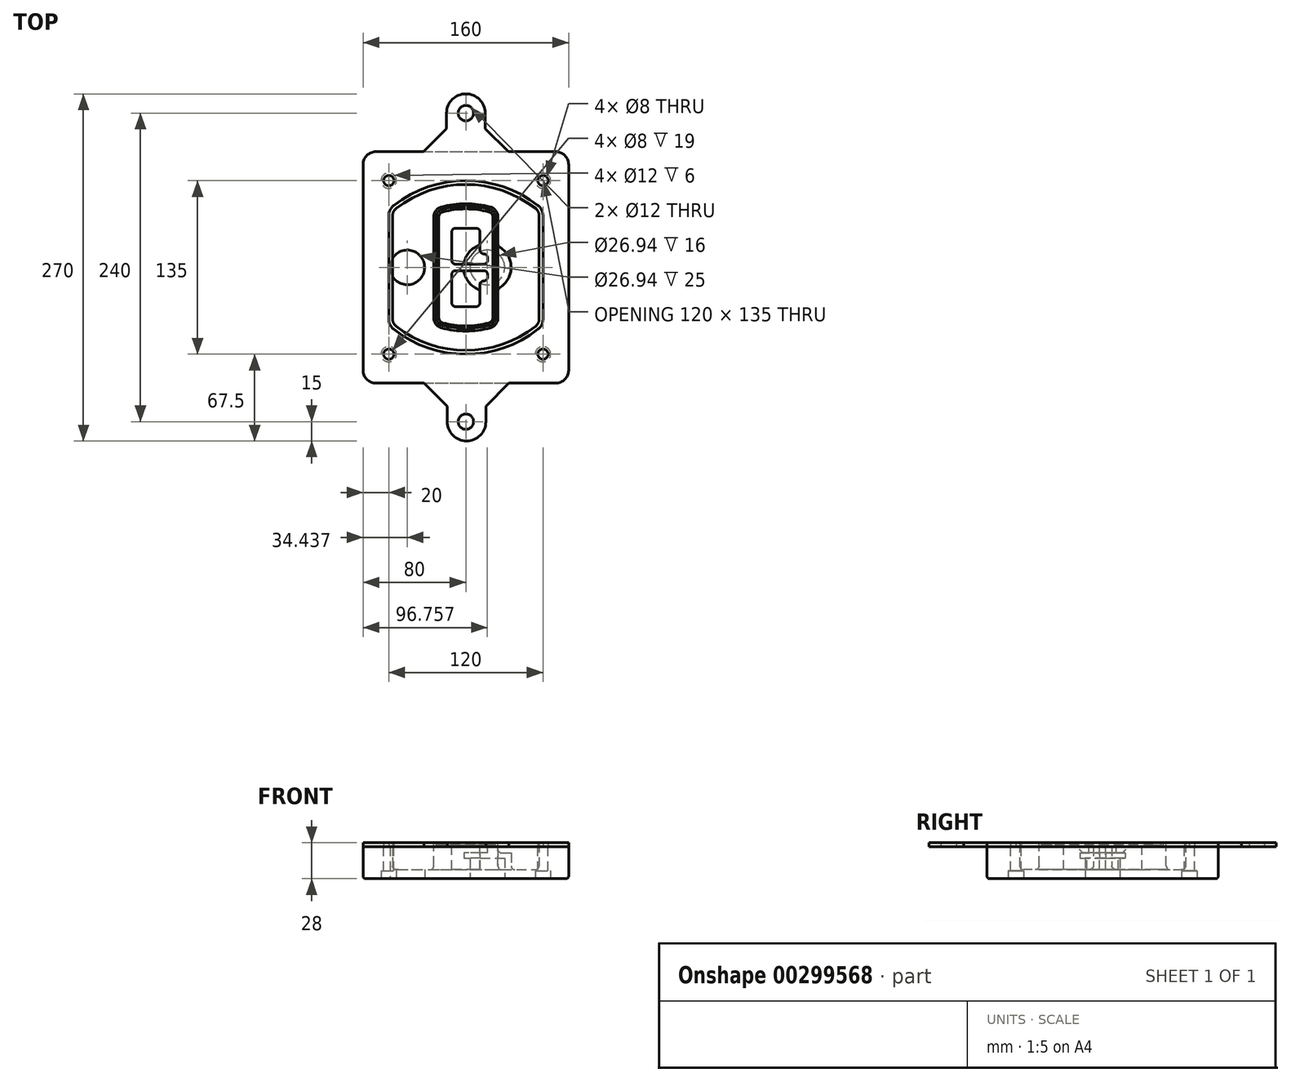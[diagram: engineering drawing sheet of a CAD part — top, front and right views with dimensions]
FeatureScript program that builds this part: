
annotation { "Feature Type Name" : "Feature", "Feature Type Description" : "" }
export const myFeature = defineFeature(function(context is Context, id is Id, definition is map)
    precondition{}
    {
        {
            var Q0;
            Q0=qCreatedBy(makeId("Top.planeOp"),FACE);
            var sketch = newSketch(context, id + "F0", { "sketchPlane" : qUnion([Q0])});
            skPoint(sketch, "E0.rect.middle", {"position": v(0, 0) * mm});
            skLineSegment(sketch, "E1.bottom", {"start": v(-70, -90) * mm, "end": v(70, -90) * mm});
            skLineSegment(sketch, "E1.top", {"start": v(-70, 90) * mm, "end": v(70, 90) * mm});
            skLineSegment(sketch, "E1.left", {"start": v(-80, -80) * mm, "end": v(-80, 80) * mm});
            skLineSegment(sketch, "E1.right", {"start": v(80, -80) * mm, "end": v(80, 80) * mm});
            skLineSegment(sketch, "E2", {"start": v(-80, 90) * mm, "end": v(80, -90) * mm, "construction": true});
            skLineSegment(sketch, "E3", {"start": v(80, 90) * mm, "end": v(-80, -90) * mm, "construction": true});
            skCircle(sketch, "E4", {"center": v(-60, 67.5) * mm, "radius": 4 * mm});
            skCircle(sketch, "E5", {"center": v(60, 67.5) * mm, "radius": 4 * mm});
            skCircle(sketch, "E6", {"center": v(60, -67.5) * mm, "radius": 4 * mm});
            skCircle(sketch, "E7", {"center": v(-60, -67.5) * mm, "radius": 4 * mm});
            skLineSegment(sketch, "E8", {"start": v(-60, 67.5) * mm, "end": v(60, 67.5) * mm, "construction": true});
            skLineSegment(sketch, "E9", {"start": v(60, 67.5) * mm, "end": v(60, -67.5) * mm, "construction": true});
            skLineSegment(sketch, "E10", {"start": v(60, -67.5) * mm, "end": v(-60, -67.5) * mm, "construction": true});
            skLineSegment(sketch, "E11", {"start": v(-60, -67.5) * mm, "end": v(-60, 67.5) * mm, "construction": true});
            skLineSegment(sketch, "E12", {"start": v(-60, 40.3) * mm, "end": v(-60, -40.3) * mm});
            skLineSegment(sketch, "E13", {"start": v(60, 40.3) * mm, "end": v(60, -40.3) * mm});
            skArc(sketch, "E14", {"start": v(56.15, 48.18) * mm, "mid": v(0, 67.5) * mm, "end": v(-56.15, 48.18) * mm});
            skArc(sketch, "E15", {"start": v(-56.15, -48.18) * mm, "mid": v(0, -67.5) * mm, "end": v(56.15, -48.18) * mm});
            skLineSegment(sketch, "E16", {"start": v(-60, 0) * mm, "end": v(60, 0) * mm, "construction": true});
            skPoint(sketch, "E17.visualSharp", {"position": v(-60, -45) * mm});
            skArc(sketch, "E17.filletArc", {"start": v(-60, -40.3) * mm, "mid": v(-58.99, -44.68) * mm, "end": v(-56.15, -48.18) * mm});
            skPoint(sketch, "E18.visualSharp", {"position": v(-60, 45) * mm});
            skArc(sketch, "E18.filletArc", {"start": v(-56.15, 48.18) * mm, "mid": v(-58.99, 44.68) * mm, "end": v(-60, 40.3) * mm});
            skPoint(sketch, "E19.visualSharp", {"position": v(60, 45) * mm});
            skArc(sketch, "E19.filletArc", {"start": v(60, 40.3) * mm, "mid": v(58.99, 44.68) * mm, "end": v(56.15, 48.18) * mm});
            skPoint(sketch, "E20.visualSharp", {"position": v(60, -45) * mm});
            skArc(sketch, "E20.filletArc", {"start": v(56.15, -48.18) * mm, "mid": v(58.99, -44.68) * mm, "end": v(60, -40.3) * mm});
            skPoint(sketch, "E21.visualSharp", {"position": v(-80, 90) * mm});
            skArc(sketch, "E21.filletArc", {"start": v(-70, 90) * mm, "mid": v(-77.07, 87.07) * mm, "end": v(-80, 80) * mm});
            skPoint(sketch, "E22.visualSharp", {"position": v(80, 90) * mm});
            skArc(sketch, "E22.filletArc", {"start": v(80, 80) * mm, "mid": v(77.07, 87.07) * mm, "end": v(70, 90) * mm});
            skPoint(sketch, "E23.visualSharp", {"position": v(80, -90) * mm});
            skArc(sketch, "E23.filletArc", {"start": v(70, -90) * mm, "mid": v(77.07, -87.07) * mm, "end": v(80, -80) * mm});
            skPoint(sketch, "E24.visualSharp", {"position": v(-80, -90) * mm});
            skArc(sketch, "E24.filletArc", {"start": v(-80, -80) * mm, "mid": v(-77.07, -87.07) * mm, "end": v(-70, -90) * mm});
            skArc(sketch, "E25.0", {"start": v(57, 40.3) * mm, "mid": v(56.3, 43.36) * mm, "end": v(54.3, 45.81) * mm});
            skLineSegment(sketch, "E25.1", {"start": v(57, 40.3) * mm, "end": v(57, -40.3) * mm});
            skArc(sketch, "E25.2", {"start": v(54.3, -45.81) * mm, "mid": v(56.3, -43.36) * mm, "end": v(57, -40.3) * mm});
            skArc(sketch, "E25.3", {"start": v(-54.3, -45.81) * mm, "mid": v(0, -64.5) * mm, "end": v(54.3, -45.81) * mm});
            skArc(sketch, "E25.4", {"start": v(-57, -40.3) * mm, "mid": v(-56.3, -43.36) * mm, "end": v(-54.3, -45.81) * mm});
            skArc(sketch, "E25.5", {"start": v(54.3, 45.81) * mm, "mid": v(0, 64.5) * mm, "end": v(-54.3, 45.81) * mm});
            skLineSegment(sketch, "E25.6", {"start": v(-57, 40.3) * mm, "end": v(-57, -40.3) * mm});
            skArc(sketch, "E25.7", {"start": v(-54.3, 45.81) * mm, "mid": v(-56.3, 43.36) * mm, "end": v(-57, 40.3) * mm});
            skArc(sketch, "E26.0", {"start": v(-58.62, 51.33) * mm, "mid": v(-62.58, 46.43) * mm, "end": v(-64, 40.3) * mm});
            skArc(sketch, "E26.1", {"start": v(58.62, 51.33) * mm, "mid": v(0, 71.5) * mm, "end": v(-58.62, 51.33) * mm});
            skArc(sketch, "E26.2", {"start": v(64, 40.3) * mm, "mid": v(62.58, 46.43) * mm, "end": v(58.62, 51.33) * mm});
            skLineSegment(sketch, "E26.3", {"start": v(64, 40.3) * mm, "end": v(64, -40.3) * mm});
            skArc(sketch, "E26.4", {"start": v(58.62, -51.33) * mm, "mid": v(62.58, -46.43) * mm, "end": v(64, -40.3) * mm});
            skLineSegment(sketch, "E26.5", {"start": v(-64, 40.3) * mm, "end": v(-64, -40.3) * mm});
            skArc(sketch, "E26.6", {"start": v(-58.62, -51.33) * mm, "mid": v(0, -71.5) * mm, "end": v(58.62, -51.33) * mm});
            skArc(sketch, "E26.7", {"start": v(-64, -40.3) * mm, "mid": v(-62.58, -46.43) * mm, "end": v(-58.62, -51.33) * mm});
            skSolve(sketch);
        }
        {
            var Q0;
            Q0=makeQuery(id+"F0.imprint","IMPRINT",FACE,{"disambiguationData":[TD([[makeQuery(id+"F0.imprint","IMPRINT",EDGE,{"derivedFrom":sQuery(id+"F0.wireOp",EDGE,"E1.bottom")}),1.0]])]});
            var Q1;
            Q1=makeQuery(id+"F0.imprint","IMPRINT",FACE,{"disambiguationData":[TD([[makeQuery(id+"F0.imprint","IMPRINT",EDGE,{"derivedFrom":sQuery(id+"F0.wireOp",EDGE,"E12")}),1.0]])]});
            var Q2;
            Q2=makeQuery(id+"F0.imprint","IMPRINT",FACE,{"disambiguationData":[TD([[makeQuery(id+"F0.imprint","IMPRINT",EDGE,{"derivedFrom":sQuery(id+"F0.wireOp",EDGE,"E25.0")}),1.0]])]});
            var Q3;
            Q3=makeQuery(id+"F0.imprint","IMPRINT",FACE,{"disambiguationData":[TD([[makeQuery(id+"F0.imprint","IMPRINT",EDGE,{"derivedFrom":sQuery(id+"F0.wireOp",EDGE,"E12")}),-1.0]])]});
            extrude(context, id + "F1", {"entities" : qUnion([Q0, Q1, Q2, Q3]), "oppositeDirection" : true, "depth" : 25 * mm});
        }
        {
            var Q0;
            Q0=makeQuery(id+"F0.imprint","IMPRINT",FACE,{"disambiguationData":[TD([[makeQuery(id+"F0.imprint","IMPRINT",EDGE,{"derivedFrom":sQuery(id+"F0.wireOp",EDGE,"E12")}),1.0]])]});
            extrude(context, id + "F2", {"entities" : qUnion([Q0]), "operationType" : NewBodyOperationType.ADD, "depth" : 3 * mm});
        }
        {
            var Q0;
            Q0=makeQuery(id+"F0.imprint","IMPRINT",FACE,{"disambiguationData":[TD([[makeQuery(id+"F0.imprint","IMPRINT",EDGE,{"derivedFrom":sQuery(id+"F0.wireOp",EDGE,"E25.0")}),1.0]])]});
            extrude(context, id + "F3", {"entities" : qUnion([Q0]), "operationType" : NewBodyOperationType.REMOVE, "oppositeDirection" : true, "depth" : 18 * mm});
        }
        {
            var Q0;
            Q0=makeQuery(id+"F2.opExtrude","CAP_FACE",FACE,{"disambiguationData":[OSD([sQuery(id+"F0.wireOp",EDGE,"E12"),sQuery(id+"F0.wireOp",EDGE,"E13"),sQuery(id+"F0.wireOp",EDGE,"E14"),sQuery(id+"F0.wireOp",EDGE,"E15"),sQuery(id+"F0.wireOp",EDGE,"E17.filletArc"),sQuery(id+"F0.wireOp",EDGE,"E18.filletArc"),sQuery(id+"F0.wireOp",EDGE,"E19.filletArc"),sQuery(id+"F0.wireOp",EDGE,"E20.filletArc"),sQuery(id+"F0.wireOp",EDGE,"E25.0"),sQuery(id+"F0.wireOp",EDGE,"E25.1"),sQuery(id+"F0.wireOp",EDGE,"E25.2"),sQuery(id+"F0.wireOp",EDGE,"E25.3"),sQuery(id+"F0.wireOp",EDGE,"E25.4"),sQuery(id+"F0.wireOp",EDGE,"E25.5"),sQuery(id+"F0.wireOp",EDGE,"E25.6"),sQuery(id+"F0.wireOp",EDGE,"E25.7")])],"isStart":false});
            var sketch = newSketch(context, id + "F4", { "sketchPlane" : qUnion([Q0])});
            skArc(sketch, "E27.0", {"start": v(-19.08, -46.97) * mm, "mid": v(0, -49.5) * mm, "end": v(19.08, -46.97) * mm});
            skArc(sketch, "E28.0", {"start": v(19.08, 46.97) * mm, "mid": v(0, 49.5) * mm, "end": v(-19.08, 46.97) * mm});
            skLineSegment(sketch, "E29", {"start": v(-25, 39.25) * mm, "end": v(-25, -39.25) * mm});
            skLineSegment(sketch, "E30", {"start": v(25, 39.25) * mm, "end": v(25, -39.25) * mm});
            skLineSegment(sketch, "E31", {"start": v(-25, 45.1) * mm, "end": v(25, 45.1) * mm, "construction": true});
            skLineSegment(sketch, "E32", {"start": v(-25, -45.1) * mm, "end": v(25, -45.1) * mm, "construction": true});
            skPoint(sketch, "E33.visualSharp", {"position": v(-25, 45.1) * mm});
            skArc(sketch, "E33.filletArc", {"start": v(-19.08, 46.97) * mm, "mid": v(-23.35, 44.11) * mm, "end": v(-25, 39.25) * mm});
            skPoint(sketch, "E34.visualSharp", {"position": v(25, 45.1) * mm});
            skArc(sketch, "E34.filletArc", {"start": v(25, 39.25) * mm, "mid": v(23.35, 44.11) * mm, "end": v(19.08, 46.97) * mm});
            skPoint(sketch, "E35.visualSharp", {"position": v(25, -45.1) * mm});
            skArc(sketch, "E35.filletArc", {"start": v(19.08, -46.97) * mm, "mid": v(23.35, -44.11) * mm, "end": v(25, -39.25) * mm});
            skPoint(sketch, "E36.visualSharp", {"position": v(-25, -45.1) * mm});
            skArc(sketch, "E36.filletArc", {"start": v(-25, -39.25) * mm, "mid": v(-23.35, -44.11) * mm, "end": v(-19.08, -46.97) * mm});
            skArc(sketch, "E37.0", {"start": v(54.3, 45.81) * mm, "mid": v(0, 64.5) * mm, "end": v(-54.3, 45.81) * mm});
            skArc(sketch, "E37.1", {"start": v(-54.3, 45.81) * mm, "mid": v(-56.3, 43.36) * mm, "end": v(-57, 40.3) * mm});
            skLineSegment(sketch, "E37.2", {"start": v(-57, 40.3) * mm, "end": v(-57, -40.3) * mm});
            skArc(sketch, "E37.3", {"start": v(-57, -40.3) * mm, "mid": v(-56.3, -43.36) * mm, "end": v(-54.3, -45.81) * mm});
            skArc(sketch, "E37.4", {"start": v(-54.3, -45.81) * mm, "mid": v(0, -64.5) * mm, "end": v(54.3, -45.81) * mm});
            skArc(sketch, "E37.5", {"start": v(54.3, -45.81) * mm, "mid": v(56.3, -43.36) * mm, "end": v(57, -40.3) * mm});
            skLineSegment(sketch, "E37.6", {"start": v(57, 40.3) * mm, "end": v(57, -40.3) * mm});
            skArc(sketch, "E37.7", {"start": v(57, 40.3) * mm, "mid": v(56.3, 43.36) * mm, "end": v(54.3, 45.81) * mm});
            skLineSegment(sketch, "E38.0", {"start": v(23, 39.25) * mm, "end": v(23, -39.25) * mm});
            skArc(sketch, "E38.1", {"start": v(18.56, -45.04) * mm, "mid": v(21.76, -42.9) * mm, "end": v(23, -39.25) * mm});
            skArc(sketch, "E38.2", {"start": v(-18.56, -45.04) * mm, "mid": v(0, -47.5) * mm, "end": v(18.56, -45.04) * mm});
            skArc(sketch, "E38.3", {"start": v(-23, -39.25) * mm, "mid": v(-21.76, -42.9) * mm, "end": v(-18.56, -45.04) * mm});
            skLineSegment(sketch, "E38.4", {"start": v(-23, 39.25) * mm, "end": v(-23, -39.25) * mm});
            skArc(sketch, "E38.5", {"start": v(23, 39.25) * mm, "mid": v(21.76, 42.9) * mm, "end": v(18.56, 45.04) * mm});
            skArc(sketch, "E38.6", {"start": v(-18.56, 45.04) * mm, "mid": v(-21.76, 42.9) * mm, "end": v(-23, 39.25) * mm});
            skArc(sketch, "E38.7", {"start": v(18.56, 45.04) * mm, "mid": v(0, 47.5) * mm, "end": v(-18.56, 45.04) * mm});
            skArc(sketch, "E39.0", {"start": v(21, 39.25) * mm, "mid": v(20.18, 41.68) * mm, "end": v(18.04, 43.1) * mm});
            skLineSegment(sketch, "E39.1", {"start": v(21, 39.25) * mm, "end": v(21, -39.25) * mm});
            skArc(sketch, "E39.2", {"start": v(18.04, -43.1) * mm, "mid": v(20.18, -41.68) * mm, "end": v(21, -39.25) * mm});
            skArc(sketch, "E39.3", {"start": v(-18.04, -43.1) * mm, "mid": v(0, -45.5) * mm, "end": v(18.04, -43.1) * mm});
            skArc(sketch, "E39.4", {"start": v(-21, -39.25) * mm, "mid": v(-20.18, -41.68) * mm, "end": v(-18.04, -43.1) * mm});
            skArc(sketch, "E39.5", {"start": v(18.04, 43.1) * mm, "mid": v(0, 45.5) * mm, "end": v(-18.04, 43.1) * mm});
            skLineSegment(sketch, "E39.6", {"start": v(-21, 39.25) * mm, "end": v(-21, -39.25) * mm});
            skArc(sketch, "E39.7", {"start": v(-18.04, 43.1) * mm, "mid": v(-20.18, 41.68) * mm, "end": v(-21, 39.25) * mm});
            skLineSegment(sketch, "E40", {"start": v(-25, 0) * mm, "end": v(25, 0) * mm, "construction": true});
            skLineSegment(sketch, "E41", {"start": v(-11, 5.5) * mm, "end": v(-11, 27.5) * mm});
            skLineSegment(sketch, "E42", {"start": v(-8, 30.5) * mm, "end": v(8, 30.5) * mm});
            skLineSegment(sketch, "E43", {"start": v(11, 27.5) * mm, "end": v(11, 13.5) * mm});
            skLineSegment(sketch, "E44", {"start": v(14, 10.5) * mm, "end": v(14, 10.5) * mm});
            skLineSegment(sketch, "E45", {"start": v(17, 7.5) * mm, "end": v(17, 5.5) * mm});
            skLineSegment(sketch, "E46", {"start": v(14, 2.5) * mm, "end": v(-8, 2.5) * mm});
            skPoint(sketch, "E47.visualSharp", {"position": v(-11, 30.5) * mm});
            skArc(sketch, "E47.filletArc", {"start": v(-8, 30.5) * mm, "mid": v(-10.12, 29.62) * mm, "end": v(-11, 27.5) * mm});
            skPoint(sketch, "E48.visualSharp", {"position": v(11, 30.5) * mm});
            skArc(sketch, "E48.filletArc", {"start": v(11, 27.5) * mm, "mid": v(10.12, 29.62) * mm, "end": v(8, 30.5) * mm});
            skPoint(sketch, "E49.visualSharp", {"position": v(11, 10.5) * mm});
            skArc(sketch, "E49.filletArc", {"start": v(11, 13.5) * mm, "mid": v(11.88, 11.38) * mm, "end": v(14, 10.5) * mm});
            skPoint(sketch, "E50.visualSharp", {"position": v(17, 10.5) * mm});
            skArc(sketch, "E50.filletArc", {"start": v(17, 7.5) * mm, "mid": v(16.12, 9.62) * mm, "end": v(14, 10.5) * mm});
            skPoint(sketch, "E51.visualSharp", {"position": v(17, 2.5) * mm});
            skArc(sketch, "E51.filletArc", {"start": v(14, 2.5) * mm, "mid": v(16.12, 3.38) * mm, "end": v(17, 5.5) * mm});
            skPoint(sketch, "E52.visualSharp", {"position": v(-11, 2.5) * mm});
            skArc(sketch, "E52.filletArc", {"start": v(-11, 5.5) * mm, "mid": v(-10.12, 3.38) * mm, "end": v(-8, 2.5) * mm});
            skLineSegment(sketch, "E53.0.MirrorCS", {"start": v(14, -2.5) * mm, "end": v(-8, -2.5) * mm});
            skArc(sketch, "E54.0.MirrorCS", {"start": v(-11, -5.5) * mm, "mid": v(-10.12, -3.38) * mm, "end": v(-8, -2.5) * mm});
            skLineSegment(sketch, "E55.0.MirrorCS", {"start": v(-11, -5.5) * mm, "end": v(-11, -27.5) * mm});
            skArc(sketch, "E56.0.MirrorCS", {"start": v(-8, -30.5) * mm, "mid": v(-10.12, -29.62) * mm, "end": v(-11, -27.5) * mm});
            skLineSegment(sketch, "E57.0.MirrorCS", {"start": v(-8, -30.5) * mm, "end": v(8, -30.5) * mm});
            skArc(sketch, "E58.0.MirrorCS", {"start": v(11, -27.5) * mm, "mid": v(10.12, -29.62) * mm, "end": v(8, -30.5) * mm});
            skLineSegment(sketch, "E59.0.MirrorCS", {"start": v(11, -27.5) * mm, "end": v(11, -13.5) * mm});
            skArc(sketch, "E60.0.MirrorCS", {"start": v(11, -13.5) * mm, "mid": v(11.88, -11.38) * mm, "end": v(14, -10.5) * mm});
            skArc(sketch, "E61.0.MirrorCS", {"start": v(17, -7.5) * mm, "mid": v(16.12, -9.62) * mm, "end": v(14, -10.5) * mm});
            skLineSegment(sketch, "E62.0.MirrorCS", {"start": v(17, -7.5) * mm, "end": v(17, -5.5) * mm});
            skArc(sketch, "E63.0.MirrorCS", {"start": v(14, -2.5) * mm, "mid": v(16.12, -3.38) * mm, "end": v(17, -5.5) * mm});
            skSolve(sketch);
        }
        {
            var Q0;
            Q0=makeQuery(id+"F4.imprint","IMPRINT",FACE,{"disambiguationData":[TD([[makeQuery(id+"F4.imprint","IMPRINT",EDGE,{"derivedFrom":sQuery(id+"F4.wireOp",EDGE,"E27.0")}),1.0]])]});
            var Q1;
            Q1=makeQuery(id+"F4.imprint","IMPRINT",FACE,{"disambiguationData":[TD([[makeQuery(id+"F4.imprint","IMPRINT",EDGE,{"derivedFrom":sQuery(id+"F4.wireOp",EDGE,"E38.0")}),-1.0]])]});
            var Q2;
            Q2=makeQuery(id+"F4.imprint","IMPRINT",FACE,{"disambiguationData":[TD([[makeQuery(id+"F4.imprint","IMPRINT",EDGE,{"derivedFrom":sQuery(id+"F4.wireOp",EDGE,"E39.0")}),1.0]])]});
            extrude(context, id + "F5", {"entities" : qUnion([Q0, Q1, Q2]), "operationType" : NewBodyOperationType.ADD, "endBound" : BoundingType.UP_TO_NEXT, "oppositeDirection" : true, "depth" : 25 * mm});
        }
        {
            var Q0;
            Q0=makeQuery(id+"F4.imprint","IMPRINT",FACE,{"disambiguationData":[TD([[makeQuery(id+"F4.imprint","IMPRINT",EDGE,{"derivedFrom":sQuery(id+"F4.wireOp",EDGE,"E38.0")}),-1.0]])]});
            extrude(context, id + "F6", {"entities" : qUnion([Q0]), "operationType" : NewBodyOperationType.REMOVE, "oppositeDirection" : true, "depth" : 2 * mm});
        }
        {
            var Q0;
            Q0=makeQuery(id+"F1.opExtrude","CAP_FACE",FACE,{"disambiguationData":[OSD([sQuery(id+"F0.wireOp",EDGE,"E1.bottom"),sQuery(id+"F0.wireOp",EDGE,"E1.top"),sQuery(id+"F0.wireOp",EDGE,"E1.left"),sQuery(id+"F0.wireOp",EDGE,"E1.right"),sQuery(id+"F0.wireOp",EDGE,"E4"),sQuery(id+"F0.wireOp",EDGE,"E5"),sQuery(id+"F0.wireOp",EDGE,"E6"),sQuery(id+"F0.wireOp",EDGE,"E7"),sQuery(id+"F0.wireOp",EDGE,"E21.filletArc"),sQuery(id+"F0.wireOp",EDGE,"E22.filletArc"),sQuery(id+"F0.wireOp",EDGE,"E23.filletArc"),sQuery(id+"F0.wireOp",EDGE,"E24.filletArc")])],"isStart":false});
            var sketch = newSketch(context, id + "F7", { "sketchPlane" : qUnion([Q0])});
            skCircle(sketch, "E64", {"center": v(16.76, 0) * mm, "radius": 13.47 * mm});
            skCircle(sketch, "E65", {"center": v(-45.56, 0) * mm, "radius": 13.47 * mm});
            skLineSegment(sketch, "E66", {"start": v(80, 0) * mm, "end": v(-80, 0) * mm});
            skCircle(sketch, "E67", {"center": v(16.76, 0) * mm, "radius": 18.47 * mm});
            skCircle(sketch, "E68", {"center": v(60, -67.5) * mm, "radius": 6 * mm});
            skCircle(sketch, "E69", {"center": v(-60, -67.5) * mm, "radius": 6 * mm});
            skCircle(sketch, "E70", {"center": v(-60, 67.5) * mm, "radius": 6 * mm});
            skCircle(sketch, "E71", {"center": v(60, 67.5) * mm, "radius": 6 * mm});
            skSolve(sketch);
        }
        {
            var Q0;
            {var subQ1=sQuery(id+"F7.wireOp",EDGE,"E66");var subQ4=sQuery(id+"F7.wireOp",EDGE,"E64");var subQ6=makeQuery(id+"F7.imprint","INTERSECT",VERTEX,{"disambiguationData":[OD(0.0)],"derivedFrom":[subQ4,subQ1]});Q0=makeQuery(id+"F7.imprint","IMPRINT",FACE,{"disambiguationData":[TD([[makeQuery(id+"F7.imprint","IMPRINT",EDGE,{"disambiguationData":[TD([[subQ6,-1.0]])],"derivedFrom":subQ4}),-1.0]])]});}
            var Q1;
            {var subQ0=sQuery(id+"F7.wireOp",EDGE,"E66");var subQ1=sQuery(id+"F7.wireOp",EDGE,"E64");var subQ3=makeQuery(id+"F7.imprint","INTERSECT",VERTEX,{"disambiguationData":[OD(0.0)],"derivedFrom":[subQ1,subQ0]});Q1=makeQuery(id+"F7.imprint","IMPRINT",FACE,{"disambiguationData":[TD([[makeQuery(id+"F7.imprint","IMPRINT",EDGE,{"disambiguationData":[TD([[subQ3,-1.0]])],"derivedFrom":subQ1}),1.0]])]});}
            var Q2;
            {var subQ0=sQuery(id+"F7.wireOp",EDGE,"E66");var subQ1=sQuery(id+"F7.wireOp",EDGE,"E64");var subQ3=makeQuery(id+"F7.imprint","INTERSECT",VERTEX,{"disambiguationData":[OD(0.0)],"derivedFrom":[subQ1,subQ0]});Q2=makeQuery(id+"F7.imprint","IMPRINT",FACE,{"disambiguationData":[TD([[makeQuery(id+"F7.imprint","IMPRINT",EDGE,{"disambiguationData":[TD([[subQ3,1.0]])],"derivedFrom":subQ1}),1.0]])]});}
            var Q3;
            {var subQ1=sQuery(id+"F7.wireOp",EDGE,"E66");var subQ4=sQuery(id+"F7.wireOp",EDGE,"E64");var subQ6=makeQuery(id+"F7.imprint","INTERSECT",VERTEX,{"disambiguationData":[OD(0.0)],"derivedFrom":[subQ4,subQ1]});Q3=makeQuery(id+"F7.imprint","IMPRINT",FACE,{"disambiguationData":[TD([[makeQuery(id+"F7.imprint","IMPRINT",EDGE,{"disambiguationData":[TD([[subQ6,1.0]])],"derivedFrom":subQ4}),-1.0]])]});}
            extrude(context, id + "F8", {"entities" : qUnion([Q0, Q1, Q2, Q3]), "operationType" : NewBodyOperationType.ADD, "oppositeDirection" : true, "depth" : 20 * mm});
        }
        {
            var Q0;
            {var subQ0=sQuery(id+"F7.wireOp",EDGE,"E66");var subQ1=sQuery(id+"F7.wireOp",EDGE,"E64");var subQ3=makeQuery(id+"F7.imprint","INTERSECT",VERTEX,{"disambiguationData":[OD(0.0)],"derivedFrom":[subQ1,subQ0]});Q0=makeQuery(id+"F7.imprint","IMPRINT",FACE,{"disambiguationData":[TD([[makeQuery(id+"F7.imprint","IMPRINT",EDGE,{"disambiguationData":[TD([[subQ3,-1.0]])],"derivedFrom":subQ1}),1.0]])]});}
            var Q1;
            {var subQ0=sQuery(id+"F7.wireOp",EDGE,"E66");var subQ1=sQuery(id+"F7.wireOp",EDGE,"E64");var subQ3=makeQuery(id+"F7.imprint","INTERSECT",VERTEX,{"disambiguationData":[OD(0.0)],"derivedFrom":[subQ1,subQ0]});Q1=makeQuery(id+"F7.imprint","IMPRINT",FACE,{"disambiguationData":[TD([[makeQuery(id+"F7.imprint","IMPRINT",EDGE,{"disambiguationData":[TD([[subQ3,1.0]])],"derivedFrom":subQ1}),1.0]])]});}
            extrude(context, id + "F9", {"entities" : qUnion([Q0, Q1]), "operationType" : NewBodyOperationType.REMOVE, "oppositeDirection" : true, "depth" : 16 * mm});
        }
        {
            var Q0;
            {var subQ0=sQuery(id+"F7.wireOp",EDGE,"E66");var subQ1=sQuery(id+"F7.wireOp",EDGE,"E65");var subQ3=makeQuery(id+"F7.imprint","INTERSECT",VERTEX,{"disambiguationData":[OD(0.0)],"derivedFrom":[subQ1,subQ0]});Q0=makeQuery(id+"F7.imprint","IMPRINT",FACE,{"disambiguationData":[TD([[makeQuery(id+"F7.imprint","IMPRINT",EDGE,{"disambiguationData":[TD([[subQ3,-1.0]])],"derivedFrom":subQ1}),1.0]])]});}
            var Q1;
            {var subQ0=sQuery(id+"F7.wireOp",EDGE,"E66");var subQ1=sQuery(id+"F7.wireOp",EDGE,"E65");var subQ3=makeQuery(id+"F7.imprint","INTERSECT",VERTEX,{"disambiguationData":[OD(0.0)],"derivedFrom":[subQ1,subQ0]});Q1=makeQuery(id+"F7.imprint","IMPRINT",FACE,{"disambiguationData":[TD([[makeQuery(id+"F7.imprint","IMPRINT",EDGE,{"disambiguationData":[TD([[subQ3,1.0]])],"derivedFrom":subQ1}),1.0]])]});}
            extrude(context, id + "F10", {"entities" : qUnion([Q0, Q1]), "operationType" : NewBodyOperationType.REMOVE, "oppositeDirection" : true, "depth" : 25 * mm});
        }
        {
            var Q0;
            Q0=makeQuery(id+"F7.imprint","IMPRINT",FACE,{"disambiguationData":[TD([[makeQuery(id+"F7.imprint","IMPRINT",EDGE,{"derivedFrom":sQuery(id+"F7.wireOp",EDGE,"E68")}),1.0]])]});
            var Q1;
            Q1=makeQuery(id+"F7.imprint","IMPRINT",FACE,{"disambiguationData":[TD([[makeQuery(id+"F7.imprint","IMPRINT",EDGE,{"derivedFrom":makeQuery(id+"F1.opExtrude","CAP_EDGE",EDGE,{"disambiguationData":[OSD([sQuery(id+"F0.wireOp",EDGE,"E5")])],"isStart":false})}),-1.0]])]});
            var Q2;
            Q2=makeQuery(id+"F7.imprint","IMPRINT",FACE,{"disambiguationData":[TD([[makeQuery(id+"F7.imprint","IMPRINT",EDGE,{"derivedFrom":sQuery(id+"F7.wireOp",EDGE,"E69")}),1.0]])]});
            var Q3;
            Q3=makeQuery(id+"F7.imprint","IMPRINT",FACE,{"disambiguationData":[TD([[makeQuery(id+"F7.imprint","IMPRINT",EDGE,{"derivedFrom":makeQuery(id+"F1.opExtrude","CAP_EDGE",EDGE,{"disambiguationData":[OSD([sQuery(id+"F0.wireOp",EDGE,"E4")])],"isStart":false})}),-1.0]])]});
            var Q4;
            Q4=makeQuery(id+"F7.imprint","IMPRINT",FACE,{"disambiguationData":[TD([[makeQuery(id+"F7.imprint","IMPRINT",EDGE,{"derivedFrom":sQuery(id+"F7.wireOp",EDGE,"E70")}),1.0]])]});
            var Q5;
            Q5=makeQuery(id+"F7.imprint","IMPRINT",FACE,{"disambiguationData":[TD([[makeQuery(id+"F7.imprint","IMPRINT",EDGE,{"derivedFrom":makeQuery(id+"F1.opExtrude","CAP_EDGE",EDGE,{"disambiguationData":[OSD([sQuery(id+"F0.wireOp",EDGE,"E7")])],"isStart":false})}),-1.0]])]});
            var Q6;
            Q6=makeQuery(id+"F7.imprint","IMPRINT",FACE,{"disambiguationData":[TD([[makeQuery(id+"F7.imprint","IMPRINT",EDGE,{"derivedFrom":sQuery(id+"F7.wireOp",EDGE,"E71")}),1.0]])]});
            var Q7;
            Q7=makeQuery(id+"F7.imprint","IMPRINT",FACE,{"disambiguationData":[TD([[makeQuery(id+"F7.imprint","IMPRINT",EDGE,{"derivedFrom":makeQuery(id+"F1.opExtrude","CAP_EDGE",EDGE,{"disambiguationData":[OSD([sQuery(id+"F0.wireOp",EDGE,"E6")])],"isStart":false})}),-1.0]])]});
            extrude(context, id + "F11", {"entities" : qUnion([Q0, Q1, Q2, Q3, Q4, Q5, Q6, Q7]), "operationType" : NewBodyOperationType.REMOVE, "oppositeDirection" : true, "depth" : 6 * mm});
        }
        {
            var Q0;
            Q0=makeQuery(id+"F9.boolean.opBoolean","COPY",FACE,{"derivedFrom":makeQuery(id+"F9.opExtrude","CAP_FACE",FACE,{"disambiguationData":[OSD([sQuery(id+"F7.wireOp",EDGE,"E64")])],"isStart":false})});
            var sketch = newSketch(context, id + "F12", { "sketchPlane" : qUnion([Q0])});
            skArc(sketch, "E72.0", {"start": v(11, 17.55) * mm, "mid": v(2.57, 11.82) * mm, "end": v(-1.54, 2.5) * mm});
            skArc(sketch, "E72.1", {"start": v(-1.54, -2.5) * mm, "mid": v(2.57, -11.82) * mm, "end": v(11, -17.55) * mm});
            skLineSegment(sketch, "E73", {"start": v(-1.54, -2.5) * mm, "end": v(14, -2.5) * mm});
            skLineSegment(sketch, "E74.0", {"start": v(14, 2.5) * mm, "end": v(-1.54, 2.5) * mm});
            skArc(sketch, "E74.1", {"start": v(14, 2.5) * mm, "mid": v(16.12, 3.38) * mm, "end": v(17, 5.5) * mm});
            skLineSegment(sketch, "E74.2", {"start": v(17, 7.5) * mm, "end": v(17, 5.5) * mm});
            skArc(sketch, "E74.3", {"start": v(17, 7.5) * mm, "mid": v(16.12, 9.62) * mm, "end": v(14, 10.5) * mm});
            skArc(sketch, "E74.4", {"start": v(11, 13.5) * mm, "mid": v(11.88, 11.38) * mm, "end": v(14, 10.5) * mm});
            skLineSegment(sketch, "E74.5", {"start": v(11, 17.55) * mm, "end": v(11, 13.5) * mm});
            skLineSegment(sketch, "E74.7", {"start": v(14, -2.5) * mm, "end": v(-1.54, -2.5) * mm});
            skArc(sketch, "E74.8", {"start": v(14, -2.5) * mm, "mid": v(16.12, -3.38) * mm, "end": v(17, -5.5) * mm});
            skLineSegment(sketch, "E74.9", {"start": v(17, -7.5) * mm, "end": v(17, -5.5) * mm});
            skArc(sketch, "E74.10", {"start": v(17, -7.5) * mm, "mid": v(16.12, -9.62) * mm, "end": v(14, -10.5) * mm});
            skArc(sketch, "E74.11", {"start": v(11, -13.5) * mm, "mid": v(11.88, -11.38) * mm, "end": v(14, -10.5) * mm});
            skLineSegment(sketch, "E74.12", {"start": v(11, -17.55) * mm, "end": v(11, -13.5) * mm});
            skPoint(sketch, "E75.orphan", {"position": v(11, -27.5) * mm});
            skPoint(sketch, "E76.orphan", {"position": v(-8, -2.5) * mm});
            skPoint(sketch, "E77.orphan", {"position": v(-8, 2.5) * mm});
            skPoint(sketch, "E78.orphan", {"position": v(11, 27.5) * mm});
            skSolve(sketch);
        }
        {
            var Q0;
            {var subQ7=sQuery(id+"F12.wireOp",EDGE,"E72.0");var subQ14=sQuery(id+"F12.wireOp",EDGE,"E72.1");var subQ16=sQuery(id+"F12.wireOp",EDGE,"E74.1");var subQ18=sQuery(id+"F12.wireOp",EDGE,"E74.8");Q0=qUnion([makeQuery(id+"F12.imprint","IMPRINT",FACE,{"disambiguationData":[TD([[makeQuery(id+"F12.imprint","IMPRINT",EDGE,{"derivedFrom":subQ7}),1.0]])]}),makeQuery(id+"F12.imprint","IMPRINT",FACE,{"disambiguationData":[TD([[makeQuery(id+"F12.imprint","IMPRINT",EDGE,{"derivedFrom":subQ14}),1.0]])]}),makeQuery(id+"F12.imprint","IMPRINT",FACE,{"disambiguationData":[TD([[makeQuery(id+"F12.imprint","IMPRINT",EDGE,{"derivedFrom":subQ16}),1.0]])]}),makeQuery(id+"F12.imprint","IMPRINT",FACE,{"disambiguationData":[TD([[makeQuery(id+"F12.imprint","IMPRINT",EDGE,{"derivedFrom":subQ18}),-1.0]])]})]);}
            var Q1;
            Q1=makeQuery(id+"F5.boolean.opBoolean","SPLIT",FACE,{"disambiguationData":[TD([makeQuery(id+"F5.opExtrude","SWEPT_FACE",FACE,{"disambiguationData":[OSD([sQuery(id+"F4.wireOp",EDGE,"E41")])]})])],"derivedFrom":makeQuery(id+"F3.boolean.opBoolean","COPY",FACE,{"derivedFrom":makeQuery(id+"F3.opExtrude","CAP_FACE",FACE,{"disambiguationData":[OSD([sQuery(id+"F0.wireOp",EDGE,"E25.0"),sQuery(id+"F0.wireOp",EDGE,"E25.1"),sQuery(id+"F0.wireOp",EDGE,"E25.2"),sQuery(id+"F0.wireOp",EDGE,"E25.3"),sQuery(id+"F0.wireOp",EDGE,"E25.4"),sQuery(id+"F0.wireOp",EDGE,"E25.5"),sQuery(id+"F0.wireOp",EDGE,"E25.6"),sQuery(id+"F0.wireOp",EDGE,"E25.7")])],"isStart":false})})});
            extrude(context, id + "F13", {"entities" : qUnion([Q0]), "operationType" : NewBodyOperationType.REMOVE, "endBound" : BoundingType.UP_TO_SURFACE, "endBoundEntityFace" : qUnion([Q1]), "depth" : 25 * mm});
        }
        {
            var Q0;
            Q0=makeQuery(id+"F3.boolean.opBoolean","COPY",EDGE,{"derivedFrom":makeQuery(id+"F3.opExtrude","CAP_EDGE",EDGE,{"disambiguationData":[OSD([sQuery(id+"F0.wireOp",EDGE,"E25.6")])],"isStart":false})});
            var Q1;
            Q1=makeQuery(id+"F8.boolean.opBoolean","INTERSECT",EDGE,{"derivedFrom":[makeQuery(id+"F5.opExtrude","SWEPT_FACE",FACE,{"disambiguationData":[OSD([sQuery(id+"F4.wireOp",EDGE,"E30")])]}),makeQuery(id+"F8.opExtrude","CAP_FACE",FACE,{"disambiguationData":[OSD([sQuery(id+"F7.wireOp",EDGE,"E67")])],"isStart":false})]});
            var Q2;
            Q2=makeQuery(id+"F8.boolean.opBoolean","INTERSECT",EDGE,{"disambiguationData":[OD(1.0)],"derivedFrom":[makeQuery(id+"F5.opExtrude","SWEPT_FACE",FACE,{"disambiguationData":[OSD([sQuery(id+"F4.wireOp",EDGE,"E30")])]}),makeQuery(id+"F8.opExtrude","SWEPT_FACE",FACE,{"disambiguationData":[OSD([sQuery(id+"F7.wireOp",EDGE,"E67")])]})]});
            var Q3;
            {var subQ0=sQuery(id+"F4.wireOp",EDGE,"E30");Q3=makeQuery(id+"F8.boolean.opBoolean","SPLIT",EDGE,{"disambiguationData":[TD([makeQuery(id+"F5.opExtrude","SWEPT_FACE",FACE,{"disambiguationData":[OSD([sQuery(id+"F4.wireOp",EDGE,"E35.filletArc")])]})])],"derivedFrom":makeQuery(id+"F5.opExtrude","CAP_EDGE",EDGE,{"disambiguationData":[OSD([subQ0])],"isStart":false})});}
            var Q4;
            {var subQ0=sQuery(id+"F0.wireOp",EDGE,"E25.7");var subQ1=sQuery(id+"F0.wireOp",EDGE,"E25.1");var subQ2=sQuery(id+"F0.wireOp",EDGE,"E25.6");var subQ3=sQuery(id+"F0.wireOp",EDGE,"E25.5");var subQ4=sQuery(id+"F0.wireOp",EDGE,"E25.4");var subQ5=sQuery(id+"F0.wireOp",EDGE,"E25.0");var subQ6=sQuery(id+"F0.wireOp",EDGE,"E25.2");var subQ7=sQuery(id+"F0.wireOp",EDGE,"E25.3");Q4=makeQuery(id+"F8.boolean.opBoolean","INTERSECT",EDGE,{"derivedFrom":[makeQuery(id+"F5.boolean.opBoolean","SPLIT",FACE,{"disambiguationData":[TD([makeQuery(id+"F2.opExtrude","SWEPT_FACE",FACE,{"disambiguationData":[OSD([subQ5])]})])],"derivedFrom":makeQuery(id+"F3.boolean.opBoolean","COPY",FACE,{"derivedFrom":makeQuery(id+"F3.opExtrude","CAP_FACE",FACE,{"disambiguationData":[OSD([subQ5,subQ1,subQ6,subQ7,subQ4,subQ3,subQ2,subQ0])],"isStart":false})})}),makeQuery(id+"F8.opExtrude","SWEPT_FACE",FACE,{"disambiguationData":[OSD([sQuery(id+"F7.wireOp",EDGE,"E67")])]})]});}
            var Q5;
            Q5=makeQuery(id+"F8.boolean.opBoolean","INTERSECT",EDGE,{"disambiguationData":[OD(0.0)],"derivedFrom":[makeQuery(id+"F5.opExtrude","SWEPT_FACE",FACE,{"disambiguationData":[OSD([sQuery(id+"F4.wireOp",EDGE,"E30")])]}),makeQuery(id+"F8.opExtrude","SWEPT_FACE",FACE,{"disambiguationData":[OSD([sQuery(id+"F7.wireOp",EDGE,"E67")])]})]});
            fillet(context, id + "F14", {"entities" : qUnion([Q0, Q1, Q2, Q3, Q4, Q5]), "radius" : 3 * mm, "tangentPropagation" : true, "allowEdgeOverflow" : false});
        }
        {
            var Q0;
            Q0=makeQuery(id+"F1.opExtrude","CAP_EDGE",EDGE,{"disambiguationData":[OSD([sQuery(id+"F0.wireOp",EDGE,"E1.bottom")])],"isStart":false});
            fillet(context, id + "F15", {"entities" : qUnion([Q0]), "radius" : 2 * mm, "tangentPropagation" : true, "allowEdgeOverflow" : false});
        }
        {
            var Q0;
            {var subQ0=sQuery(id+"F0.wireOp",EDGE,"E21.filletArc");var subQ1=sQuery(id+"F0.wireOp",EDGE,"E7");var subQ2=sQuery(id+"F0.wireOp",EDGE,"E6");var subQ3=sQuery(id+"F0.wireOp",EDGE,"E5");var subQ4=sQuery(id+"F0.wireOp",EDGE,"E4");var subQ5=sQuery(id+"F0.wireOp",EDGE,"E22.filletArc");var subQ6=sQuery(id+"F0.wireOp",EDGE,"E1.bottom");var subQ7=sQuery(id+"F0.wireOp",EDGE,"E1.right");var subQ8=sQuery(id+"F0.wireOp",EDGE,"E1.top");var subQ9=sQuery(id+"F0.wireOp",EDGE,"E1.left");var subQ10=sQuery(id+"F0.wireOp",EDGE,"E23.filletArc");var subQ11=sQuery(id+"F0.wireOp",EDGE,"E24.filletArc");Q0=makeQuery(id+"F2.boolean.opBoolean","SPLIT",FACE,{"disambiguationData":[TD([makeQuery(id+"F1.opExtrude","SWEPT_FACE",FACE,{"disambiguationData":[OSD([subQ6])]})])],"derivedFrom":makeQuery(id+"F1.opExtrude","CAP_FACE",FACE,{"disambiguationData":[OSD([subQ6,subQ8,subQ9,subQ7,subQ4,subQ3,subQ2,subQ1,subQ0,subQ5,subQ10,subQ11])],"isStart":true})});}
            var sketch = newSketch(context, id + "F16", { "sketchPlane" : qUnion([Q0])});
            skArc(sketch, "E79", {"start": v(15, 120) * mm, "mid": v(0, 135) * mm, "end": v(-15, 120) * mm});
            skLineSegment(sketch, "E80", {"start": v(-15, 120) * mm, "end": v(-15, 108) * mm});
            skLineSegment(sketch, "E81", {"start": v(15, 120) * mm, "end": v(15, 108) * mm});
            skLineSegment(sketch, "E82", {"start": v(-15, 108) * mm, "end": v(-33, 90) * mm});
            skLineSegment(sketch, "E83", {"start": v(15, 108) * mm, "end": v(33, 90) * mm});
            skCircle(sketch, "E84", {"center": v(0, 120) * mm, "radius": 6 * mm});
            skLineSegment(sketch, "E85", {"start": v(0, 120) * mm, "end": v(0, 90) * mm, "construction": true});
            skLineSegment(sketch, "E86", {"start": v(0, -90) * mm, "end": v(0, -120) * mm, "construction": true});
            skCircle(sketch, "E87", {"center": v(0, -120) * mm, "radius": 6 * mm});
            skLineSegment(sketch, "E88", {"start": v(0.57, -120) * mm, "end": v(0.57, -120) * mm});
            skLineSegment(sketch, "E89", {"start": v(0.57, -120) * mm, "end": v(0.57, -108) * mm});
            skArc(sketch, "E90", {"start": v(-14.43, -120) * mm, "mid": v(0.57, -135) * mm, "end": v(15.57, -120) * mm});
            skLineSegment(sketch, "E91", {"start": v(15.57, -120) * mm, "end": v(15.57, -108) * mm});
            skLineSegment(sketch, "E92", {"start": v(15.57, -108) * mm, "end": v(33.57, -90) * mm});
            skLineSegment(sketch, "E93", {"start": v(-14.43, -120) * mm, "end": v(-14.43, -108) * mm});
            skLineSegment(sketch, "E94", {"start": v(-14.43, -108) * mm, "end": v(-32.43, -90) * mm});
            skSolve(sketch);
        }
        {
            var Q0;
            Q0=makeQuery(id+"F16.imprint","IMPRINT",FACE,{"disambiguationData":[TD([[makeQuery(id+"F16.imprint","IMPRINT",EDGE,{"derivedFrom":sQuery(id+"F16.wireOp",EDGE,"E87")}),-1.0]])]});
            var Q1;
            Q1=makeQuery(id+"F16.imprint","IMPRINT",FACE,{"disambiguationData":[TD([[makeQuery(id+"F16.imprint","IMPRINT",EDGE,{"derivedFrom":sQuery(id+"F16.wireOp",EDGE,"E79")}),1.0]])]});
            var Q2;
            Q2=makeQuery(id+"F16.imprint","IMPRINT",FACE,{"disambiguationData":[TD([[makeQuery(id+"F16.imprint","IMPRINT",EDGE,{"derivedFrom":makeQuery(id+"F1.opExtrude","CAP_EDGE",EDGE,{"disambiguationData":[OSD([sQuery(id+"F0.wireOp",EDGE,"E1.left")])],"isStart":true})}),-1.0]])]});
            var Q3;
            Q3=makeQuery(id+"F2.opExtrude","CAP_FACE",FACE,{"disambiguationData":[OSD([sQuery(id+"F0.wireOp",EDGE,"E12"),sQuery(id+"F0.wireOp",EDGE,"E13"),sQuery(id+"F0.wireOp",EDGE,"E14"),sQuery(id+"F0.wireOp",EDGE,"E15"),sQuery(id+"F0.wireOp",EDGE,"E17.filletArc"),sQuery(id+"F0.wireOp",EDGE,"E18.filletArc"),sQuery(id+"F0.wireOp",EDGE,"E19.filletArc"),sQuery(id+"F0.wireOp",EDGE,"E20.filletArc"),sQuery(id+"F0.wireOp",EDGE,"E25.0"),sQuery(id+"F0.wireOp",EDGE,"E25.1"),sQuery(id+"F0.wireOp",EDGE,"E25.2"),sQuery(id+"F0.wireOp",EDGE,"E25.3"),sQuery(id+"F0.wireOp",EDGE,"E25.4"),sQuery(id+"F0.wireOp",EDGE,"E25.5"),sQuery(id+"F0.wireOp",EDGE,"E25.6"),sQuery(id+"F0.wireOp",EDGE,"E25.7")])],"isStart":false});
            extrude(context, id + "F17", {"entities" : qUnion([Q0, Q1, Q2]), "endBound" : BoundingType.UP_TO_SURFACE, "endBoundEntityFace" : qUnion([Q3]), "depth" : 25 * mm});
        }
    });
